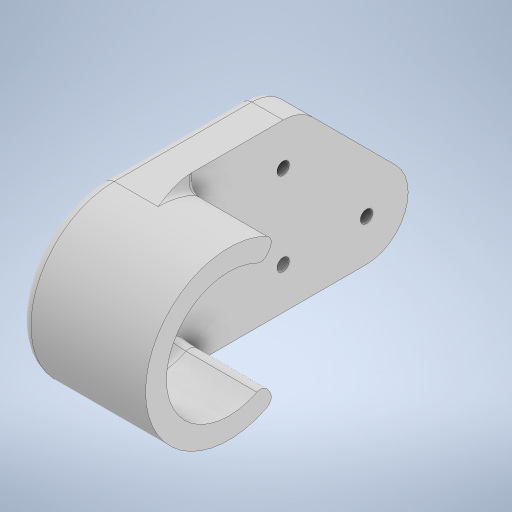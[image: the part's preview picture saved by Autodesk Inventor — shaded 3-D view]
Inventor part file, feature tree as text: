
AUTODESK INVENTOR PART (.ipt)
format: ipt  version: 2024 (Build 280153000, 153)  size: 1,015,296 bytes
history: native  units: in
note: dims shown in document units (in); Inventor stores cm internally (conversion verified against a paired STEP export)
features: extrude x9, sketch x7, fillet x7, chamfer x1, plane x1, projected_geometry x1
ambient origin geometry x8: Origin, YZ Plane, XZ Plane, XY Plane, X Axis, Y Axis, Z Axis, Center Point
bodies: Solid1 (feature_tree)
feature tree (26):
  extrude  "Extrusion1"  Depth=0.5in
  sketch  "Sketch2"  dims[d4=2.5in d6=5.5in]
  extrude  "Extrusion4"  Depth=5.5in
  extrude  "Extrusion5"  Depth=0.5in
  fillet  "Fillet2"  Radius=0.5in
  chamfer  "Chamfer1"  Distance=2.0in
  fillet  "Fillet3"  Radius=2.0in
  sketch  "Sketch3"  dims[d7=2.0in d8=1.04in d9=0.5in]
  extrude  "Extrusion6"  Depth=0.15in
  extrude  "Extrusion7"  Depth=0.125in
  fillet  "Fillet4"  Radius=0.35in
  extrude  "Extrusion8"  Depth=0.125in
  extrude  "Extrusion9"  Depth=0.125in
  extrude  "Extrusion10"  Depth=1.0in
  fillet  "Fillet5"  Radius=1.0in
  fillet  "Fillet6"  Radius=0.4in
  fillet  "Fillet7"  [1 undecoded]
  plane  "Work Plane1"
  sketch  "Sketch6"  dims[d17=2.5in d32=0.15in]
  extrude  "Extrusion11"  Depth=0.125in TaperAngle=0.0deg
  fillet  "Fillet9"  Radius=0.1in
  sketch  "Sketch1"  dims[d1=0.35in d3=0.5in]
  sketch  "Sketch4"  dims[d10=4.0in]
  sketch  "Sketch5"  dims[d13=1.25in d14=2.0in d15=0.0in d16=2.0in]
  projected_geometry  "Projected Loop1"
  sketch  "Sketch7"  dims[d34=0.15in d36=0.15in d38=0.35in d39=0.35in d40=0.35in d41=1.0in d42=1.0in d43=0.4in d44=0.0in d45=0.0in d46=0.3in d47=0.0in d48=0.1in d49=0.5in d50=0.5in d51=0.5in d52=1.0in d53=0.125in d54=45.0deg d55=0.5in d56=1.25in d57=0.1in d58=0.35in d59=0.1in d60=0.35in d61=0.1in d62=0.3in d63=0.1in d64=0.3in d65=0.25in d66=0.25in d67=0.25in d68=0.25in d69=0.25in d70=0.0in d71=0.0in d72=0.35in d73=0.0in d74=0.05in d75=0.35in d76=0.0in d77=1.1in d78=1.5in d79=1.0in d80=0.0in d81=0.0in d82=0.0in d83=0.15in d84=0.15in d85=0.1in d87=0.0in d88=0.0in d89=0.125in]
note: 1 required parameter value undecoded (feature->parameter linkage not recoverable at this tier; creation-order binding heuristic only, values carry confidence <= 0.55)
